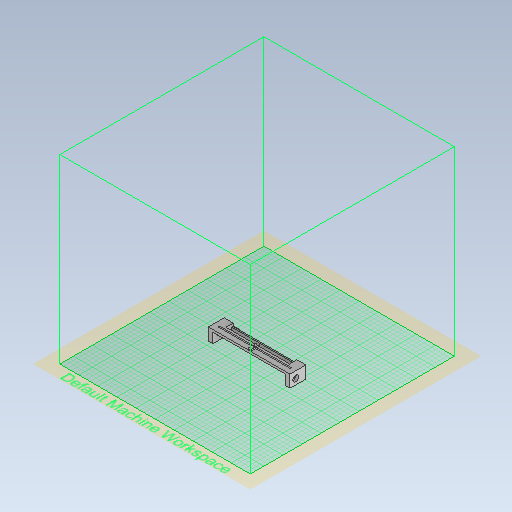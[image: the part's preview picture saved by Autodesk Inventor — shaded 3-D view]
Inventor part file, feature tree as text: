
AUTODESK INVENTOR PART (.ipt)
format: ipt  version: 2020 (Build 240168000, 168)  size: 496,128 bytes
history: native  units: mm
features: sketch x22, extrude x15, fillet x1
ambient origin geometry x8: Origin, YZ Plane, XZ Plane, XY Plane, X Axis, Y Axis, Z Axis, Center Point
bodies: Solid1 (feature_tree)
feature tree (38):
  extrude  "Extrusion1"  Depth=27.0mm
  extrude  "Extrusion2"  Depth=25.0mm
  sketch  "Sketch3"  dims[d4=10.0mm d5=0.0mm d6=10.0mm]
  sketch  "Sketch4"  dims[d7=10.0mm d8=0.0mm d9=5.0mm]
  sketch  "Sketch5"  dims[d10=11.0mm d11=5.0mm]
  extrude  "Extrusion3"  Depth=10.0mm
  extrude  "Extrusion4"  Depth=5.0mm
  extrude  "Extrusion5"  Depth=5.0mm
  extrude  "Extrusion6"  Depth=10.0mm
  fillet  "Fillet1"  Radius=7.5mm
  extrude  "Extrusion7"  Depth=10.0mm TaperAngle=0.0deg
  sketch  "Sketch11"  dims[d28=3.0mm d29=12.0mm]
  extrude  "Extrusion8"  Depth=7.0mm
  sketch  "Sketch13"  dims[d33=41.275mm d34=7.0mm]
  extrude  "Extrusion9"  Depth=3.0mm
  extrude  "Extrusion10"  Depth=12.0mm
  sketch  "Sketch16"  dims[d42=2.0mm]
  extrude  "Extrusion11"  Depth=12.0mm
  sketch  "Sketch18"  dims[d45=15.0mm d46=0.0mm]
  extrude  "Extrusion12"  Depth=23.5mm TaperAngle=0.0deg
  extrude  "Extrusion13"  Depth=7.0mm
  extrude  "Extrusion14"  Depth=7.0mm
  extrude  "Extrusion15"  Depth=19.0mm TaperAngle=0.0deg
  sketch  "Sketch1"  dims[d0=35.0mm d1=27.0mm]
  sketch  "Sketch2"  dims[d2=25.0mm d3=12.7mm]
  sketch  "Sketch6"  dims[d12=150.0mm d13=0.0mm d14=10.0mm d15=7.5mm d16=0.0mm]
  sketch  "Sketch7"  dims[d17=10.0mm d18=0.0mm d19=10.0mm d20=0.0mm]
  sketch  "Sketch8"  dims[d21=2.0mm d22=7.0mm]
  sketch  "Sketch9"  dims[d23=14.0mm d24=3.0mm]
  sketch  "Sketch10"  dims[d25=140.0mm d26=0.0mm d27=12.0mm]
  sketch  "Sketch12"  dims[d30=3.0mm d31=23.5mm d32=0.0mm]
  sketch  "Sketch14"  dims[d35=4.5mm d36=0.0mm d37=7.0mm]
  sketch  "Sketch15"  dims[d38=4.5mm d39=0.0mm d40=19.0mm d41=0.0mm]
  sketch  "Sketch17"  dims[d43=19.0mm d44=0.0mm]
  sketch  "Sketch19"  dims[d47=6.4mm]
  sketch  "Sketch20"  dims[d48=15.0mm d49=0.0mm]
  sketch  "Sketch21"  dims[d50=20.0mm]
  sketch  "Sketch22"  dims[d51=15.0mm d52=6.4mm d53=6.5mm d54=0.0mm]
